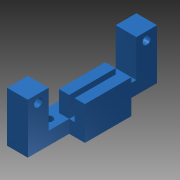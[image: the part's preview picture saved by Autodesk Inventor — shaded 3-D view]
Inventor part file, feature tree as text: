
AUTODESK INVENTOR PART (.ipt)
format: ipt  version: 2013 (Build 170138000, 138)  size: 133,632 bytes
history: native  units: mm
features: extrude x4, sketch x4
ambient origin geometry x8: Origin, YZ Plane, XZ Plane, XY Plane, X Axis, Y Axis, Z Axis, Center Point
bodies: Solid1 (feature_tree)
feature tree (8):
  extrude  "Extrusion1"  Depth=50.0mm
  extrude  "Extrusion2"  Depth=3.2mm
  extrude  "Extrusion3"  Depth=8.0mm
  extrude  "Extrusion4"  Depth=14.4mm TaperAngle=0.0deg
  sketch  "Sketch1"  dims[d0=8.0mm d1=50.0mm]
  sketch  "Sketch2"  dims[d2=3.2mm d3=3.2mm]
  sketch  "Sketch3"  dims[d6=5.0mm d7=0.0mm d8=8.0mm]
  sketch  "Sketch4"  dims[d10=8.0mm d11=14.4mm d12=0.0mm d13=3.2mm d14=3.2mm d15=3.0mm d16=15.0mm d17=0.0mm d18=6.1mm d19=18.0mm d21=4.0mm d23=8.0mm d24=0.0mm d26=4.0mm d27=2.1mm d28=4.0mm d29=4.0mm]
